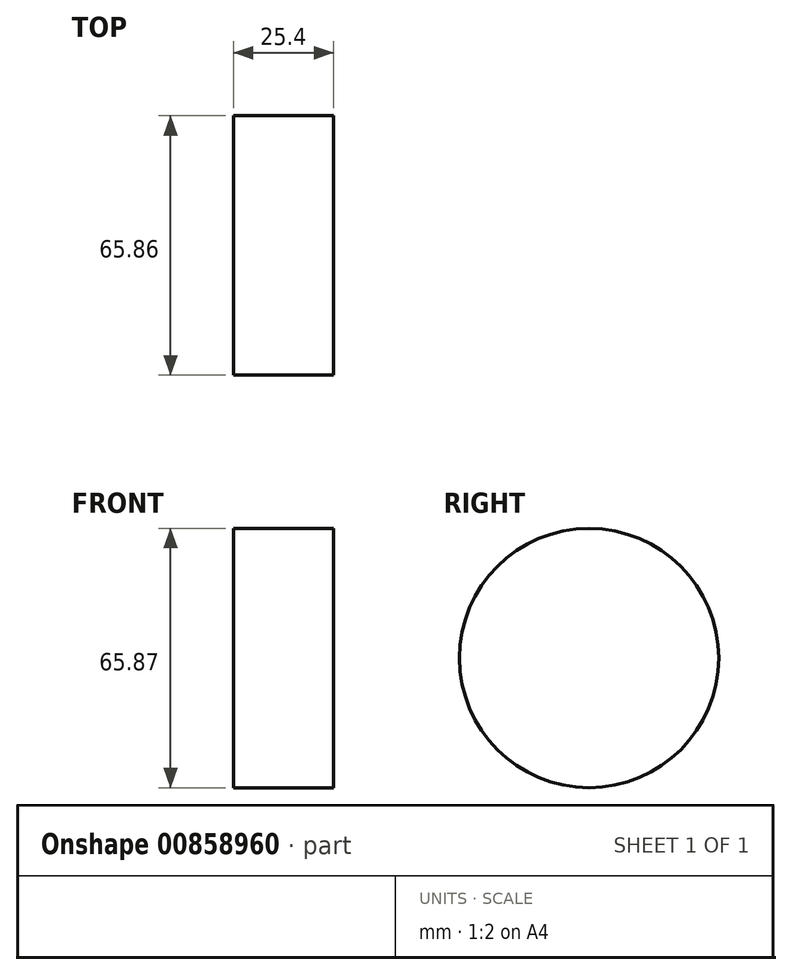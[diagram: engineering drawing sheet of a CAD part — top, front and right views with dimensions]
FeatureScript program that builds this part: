
annotation { "Feature Type Name" : "Feature", "Feature Type Description" : "" }
export const myFeature = defineFeature(function(context is Context, id is Id, definition is map)
    precondition{}
    {
        {
            var Q0;
            Q0=qCreatedBy(makeId("Right.planeOp"),FACE);
            var sketch = newSketch(context, id + "F0", { "sketchPlane" : qUnion([Q0])});
            skCircle(sketch, "E0", {"center": v(0, 13.65) * mm, "radius": 64.74 * mm});
            skCircle(sketch, "E1", {"center": v(0, 44.98) * mm, "radius": 32.93 * mm});
            skSolve(sketch);
        }
        {
            var Q0;
            Q0=makeQuery(id+"F0.imprint","IMPRINT",FACE,{"disambiguationData":[TD([[makeQuery(id+"F0.imprint","IMPRINT",EDGE,{"derivedFrom":sQuery(id+"F0.wireOp",EDGE,"E1")}),1.0]])]});
            extrude(context, id + "F1", {"entities" : qUnion([Q0]), "depth" : 25.4 * mm, "offsetDistance" : 25.4 * mm});
        }
    });
